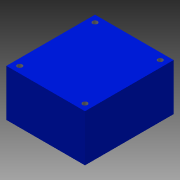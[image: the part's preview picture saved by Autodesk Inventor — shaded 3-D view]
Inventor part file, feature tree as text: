
AUTODESK INVENTOR PART (.ipt)
format: ipt  version: 2015 (Build 190159000, 159)  size: 96,256 bytes
history: native  units: mm
features: sketch x2, other x1, extrude x1, hole x1
ambient origin geometry x8: Origin, YZ Plane, XZ Plane, XY Plane, X Axis, Y Axis, Z Axis, Center Point
bodies: Body1 (feature_tree)
feature tree (5):
  other  "ソリッド1"
  extrude  "押し出し1"  Depth=47.0mm
  hole  "穴1"  [1 undecoded]
  sketch  "スケッチ1"
  sketch  "スケッチ2"
note: 1 required parameter value undecoded (feature->parameter linkage not recoverable at this tier; creation-order binding heuristic only, values carry confidence <= 0.55)
